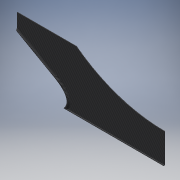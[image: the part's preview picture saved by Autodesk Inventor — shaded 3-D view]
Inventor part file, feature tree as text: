
AUTODESK INVENTOR PART (.ipt)
format: ipt  version: 2018 (Build 220112000, 112)  size: 188,928 bytes
history: native  units: mm
features: extrude x3, other x2, sketch x2, fillet x1, shell x1
ambient origin geometry x8: Origin, YZ Plane, XZ Plane, XY Plane, X Axis, Y Axis, Z Axis, Center Point
bodies: Body1 (feature_tree)
feature tree (9):
  other  "ソリッド1"
  extrude  "押し出し1"  Depth=500.0mm
  other  "作業平面1"
  extrude  "押し出し2"  Depth=200.0mm
  fillet  "フィレット1"  Radius=5.0mm
  shell  "シェル1"  Thickness=150.0deg
  extrude  "押し出し3"  Depth=20.0mm TaperAngle=0.0deg
  sketch  "スケッチ1"
  sketch  "スケッチ3"
